# Revit family: Legrand_Enveloppes_industrielles_Metal_Armoires_Atlantic_Version_horizontale
name_source: partatom
category: Equipement électrique
revit_build: Autodesk Revit 2018 (Build: 20170223_1515(x64)
units: mm (PartAtom-declared; Revit-internal decimal feet)

## family parameters
Basée sur le plan de construction = Non
Configuration du panneau = Deux colonnes, circuits au sein
Cote de connecteur circulaire = Utiliser le diamètre
Couper avec des vides une fois chargée = Non
Numéro OmniClass = 23.80.30.11.17
Partagée = Non
Point de calcul de pièce = Non
Titre OmniClass = Distribution Boards and Control Panels
Toujours verticalement = Oui
Type d'élément = Tableau de raccordement

## types (7) — shared parameters
Conditions Générale d'Utilisation = https://export.legrand.com
ETIM Class 6.0 = EC000058
Fabricant = Legrand
IK = 10
IP = 66
Image du type = Atlantic_carrée_035505_pw_234051_pz_18.jpg
Matière = Polyester
Poids = 0.00 kg
RAL = 7035
URL = www.legrand.fr

## per-type parameters (varying)
| type | Coffret 035501 | Coffret 035506 | Coffret 035521 | Coffret 035533 | Coffret 035534 | Coffret 035537 | Coffret 035590 | Description | Hauteur | Largeur | distance avant zone d'installation | distance coté zone d'installation | largeur zone d'installation | profondeur | profondeur zone d'installation |
| Legrand_Enveloppes_industrielles_Metal_Armoires_Atlantic_Version_horizontale  035501 | Oui | Non | Non | Non | Non | Non | Non | Ref 035501 - Legrand_Enveloppes_industrielles_Metal_Armoires_Atlantic_Version_horizontale | 300 mm | 400 mm  [stored 1.31234 ft] | 400 mm  [stored 1.31234 ft] | 200 mm  [stored 0.656168 ft] | 800 mm  [stored 2.62467 ft] | 200 mm  [stored 0.656168 ft] | 600 mm |
| Legrand_Enveloppes_industrielles_Metal_Armoires_Atlantic_Version_horizontale  035506 | Non | Oui | Non | Non | Non | Non | Non | Ref 035506 - Legrand_Enveloppes_industrielles_Metal_Armoires_Atlantic_Version_horizontale | 400 mm  [stored 1.31234 ft] | 600 mm | 600 mm | 250 mm  [stored 0.82021 ft] | 1100 mm | 250 mm  [stored 0.82021 ft] | 850 mm  [stored 2.78871 ft] |
| Legrand_Enveloppes_industrielles_Metal_Armoires_Atlantic_Version_horizontale  035521 | Non | Non | Oui | Non | Non | Non | Non | Ref 035521 - Legrand_Enveloppes_industrielles_Metal_Armoires_Atlantic_Version_horizontale | 600 mm | 800 mm  [stored 2.62467 ft] | 800 mm  [stored 2.62467 ft] | 300 mm | 1400 mm  [stored 4.59318 ft] | 300 mm | 1100 mm |
| Legrand_Enveloppes_industrielles_Metal_Armoires_Atlantic_Version_horizontale  035533 | Non | Non | Non | Oui | Non | Non | Non | Ref 035533 - Legrand_Enveloppes_industrielles_Metal_Armoires_Atlantic_Version_horizontale | 800 mm  [stored 2.62467 ft] | 1000 mm  [stored 3.28084 ft] | 1000 mm  [stored 3.28084 ft] | 250 mm  [stored 0.82021 ft] | 1500 mm  [stored 4.92126 ft] | 250 mm  [stored 0.82021 ft] | 1250 mm  [stored 4.10105 ft] |
| Legrand_Enveloppes_industrielles_Metal_Armoires_Atlantic_Version_horizontale  035534 | Non | Non | Non | Non | Oui | Non | Non | Ref 035534 - Legrand_Enveloppes_industrielles_Metal_Armoires_Atlantic_Version_horizontale | 800 mm  [stored 2.62467 ft] | 1000 mm  [stored 3.28084 ft] | 1000 mm  [stored 3.28084 ft] | 300 mm | 1600 mm  [stored 5.24934 ft] | 300 mm | 1300 mm  [stored 4.26509 ft] |
| Legrand_Enveloppes_industrielles_Metal_Armoires_Atlantic_Version_horizontale  035537 | Non | Non | Non | Non | Non | Oui | Non | Ref 035537 - Legrand_Enveloppes_industrielles_Metal_Armoires_Atlantic_Version_horizontale | 600 mm | 1000 mm  [stored 3.28084 ft] | 1000 mm  [stored 3.28084 ft] | 300 mm | 1600 mm  [stored 5.24934 ft] | 300 mm | 1300 mm  [stored 4.26509 ft] |
| Legrand_Enveloppes_industrielles_Metal_Armoires_Atlantic_Version_horizontale  035590 | Non | Non | Non | Non | Non | Non | Oui | Ref 035590 - Legrand_Enveloppes_industrielles_Metal_Armoires_Atlantic_Version_horizontale | 1000 mm  [stored 3.28084 ft] | 1200 mm | 1200 mm | 300 mm | 1800 mm  [stored 5.90551 ft] | 300 mm | 1500 mm  [stored 4.92126 ft] |

note: [stored X ft] marks values corroborated as IEEE doubles in the binary element streams (Revit-internal decimal feet)
